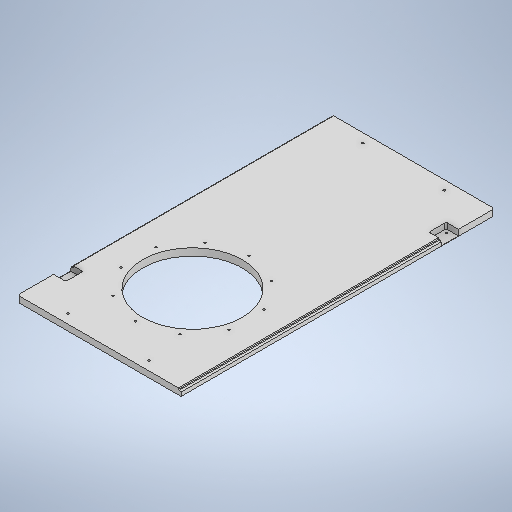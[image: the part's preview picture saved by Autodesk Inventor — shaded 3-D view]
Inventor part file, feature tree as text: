
AUTODESK INVENTOR PART (.ipt)
format: ipt  version: 2025.2 (Build 292293000, 293)  size: 384,000 bytes
history: native  units: in
note: dims shown in document units (in); Inventor stores cm internally (conversion verified against a paired STEP export)
features: sketch x9, chamfer x5, extrude x4, hole x3, plane x2, fillet x1
ambient origin geometry x8: Origin, YZ Plane, XZ Plane, XY Plane, X Axis, Y Axis, Z Axis, Center Point
bodies: Solid1 (feature_tree)
feature tree (24):
  extrude  "Extrusion1"  Depth=27.1654in
  sketch  "Sketch2"  dims[d2=0.625in d3=0.0in d4=8.0709in]
  extrude  "Extrusion2"  Depth=0.625in
  plane  "Work Plane1"
  hole  "Hole3"  [1 undecoded]
  sketch  "Sketch7"  dims[d56=25.5906in]
  plane  "Work Plane2"
  hole  "Hole4"  [1 undecoded]
  sketch  "Sketch9"  dims[d64=10.3543in]
  fillet  "Fillet2"  Radius=7.0625in
  chamfer  "Chamfer1"  Distance=1.063in
  chamfer  "Chamfer2"  Distance=1.063in
  extrude  "Extrusion7"  Depth=1.4961in
  extrude  "Extrusion8"  Depth=1.4961in
  chamfer  "Chamfer3"  Distance=3.1102in
  chamfer  "Chamfer4"  Distance=3.1102in
  hole  "Hole5"  [1 undecoded]
  chamfer  "Chamfer5"  Distance=0.0984in Angle=45.0deg
  sketch  "Sketch1"  dims[d0=14.1732in d1=27.1654in]
  sketch  "Sketch6"  dims[d8=10.6299in d50=5.9055in d55=7.0625in]
  sketch  "Sketch8"  dims[d57=0.1936in d58=0.1969in d59=0.1575in d60=0.0787in d61=90.0deg d62=0.1969in d63=0.8108in]
  sketch  "Sketch10"  dims[d65=10.6299in]
  sketch  "Sketch11"  dims[d68=9.8425in d74=0.1628in d75=0.3937in d76=0.1575in d77=0.0787in d78=90.0deg d79=0.3937in d80=0.8108in d82=1.063in d83=1.063in d84=1.4961in d85=1.4961in d86=3.1102in d87=3.1102in d88=0.1969in d89=0.0984in d90=0.0787in d91=45.0deg d92=0.0984in d93=0.0787in d94=45.0deg d95=0.1181in d96=0.1181in d97=0.4951in d98=0.0in d99=0.2362in d100=0.2362in d101=0.122in d102=0.0in d103=0.0787in d104=0.1378in d105=45.0deg d106=0.1378in d107=0.0787in d108=45.0deg d109=0.748in d110=0.315in d111=0.8661in d112=0.748in d113=0.1299in d114=0.1299in d115=0.1299in d116=0.1299in d118=0.315in d119=0.8661in d120=0.748in d121=0.748in d122=0.1276in d123=0.315in d124=0.1575in d125=0.0787in d126=90.0deg d127=0.315in d128=0.8108in d129=0.0138in d130=0.0787in d131=45.0deg d146=0.1969in d147=3.937in d149=360.0deg d26=0.0394in d27=0.0394in d28=0.0394in d29=0.0059in d30=0.0098in d31=0.0148in d32=0.5635in d33=0.0295in d34=0.8108in d35=0.0025in d36=0.0295in d37=0.0148in d66=0.0197in d67=0.0344in]
  sketch  "Sketch Circular Pattern5"  dims[d5=8.6614in d6=0.0in d7=0.0in]
note: 3 required parameter values undecoded (feature->parameter linkage not recoverable at this tier; creation-order binding heuristic only, values carry confidence <= 0.55)
